# Revit family: Torro
name_source: partatom
category: Мебель
revit_build: Autodesk Revit 2017 (Build: 20160225_1515(x64)
units: mm (PartAtom-declared; Revit-internal decimal feet)

## family parameters
Всегда вертикально = Да
Заголовок OmniClass = General Furniture and Specialties
На основе рабочей плоскости = Нет
Номер OmniClass = 23.40.20.00
Общий = Нет
При загрузке вырезать с полостями = Нет
Точка расчета площади = Нет

## types (4) — shared parameters
Fabric Seat = Нет
Fabric Seat Material = Skandiform Fabric 1
Leg = Skandiform Chrome
Изготовитель = Skandiform AB
Ключевая пометка = XBF.2
Комментарии к типоразмеру = Created by Astacus AB
Описание = Chassis in chromium. Armrests in polyurehane

## per-type parameters (varying)
| type | Armrest | Seat | URL | Группа модели |
| S-020 | Нет | Skandiform Wood | http://www.biminfo.se | S-020 |
| KS-120 | Да | Skandiform Wood | http://file-system.ru | KS-120 |
| S-021 | Нет | Skandiform Fabric 1 | http://www.biminfo.se | S-020 |
| KS-121 | Да | Skandiform Fabric 1 | http://www.biminfo.se | S-020 |

## geometry (parser evidence)
native form markers: Blend x3, Sweep x7
no freeform markers — native parametric forms only
